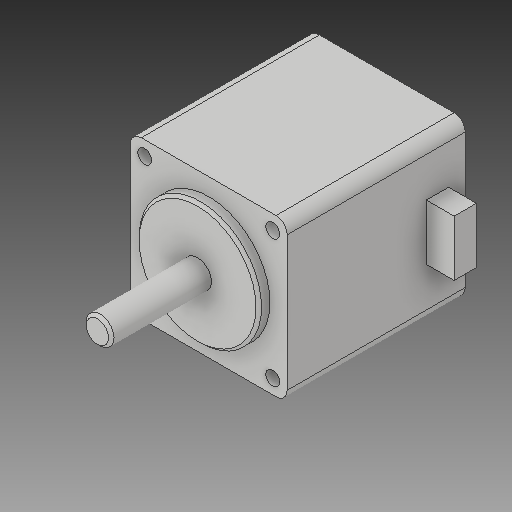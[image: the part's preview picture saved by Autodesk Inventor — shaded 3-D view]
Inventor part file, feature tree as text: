
AUTODESK INVENTOR PART (.ipt)
format: ipt  version: 2019 (Build 230136000, 136)  size: 180,736 bytes
history: native  units: mm
features: extrude x5, sketch x5, chamfer x2, fillet x1
ambient origin geometry x8: Origin, YZ Plane, XZ Plane, XY Plane, X Axis, Y Axis, Z Axis, Center Point
bodies: Solid1 (feature_tree)
feature tree (13):
  extrude  "Extrusion1"  Depth=28.2mm
  extrude  "Extrusion2"  Depth=32.0mm
  extrude  "Extrusion3"  Depth=2.5mm
  extrude  "Extrusion4"  Depth=4.5mm TaperAngle=0.0deg
  fillet  "Fillet1"  Radius=22.0mm
  chamfer  "Chamfer1"  Distance=2.0mm
  chamfer  "Chamfer2"  Distance=18.0mm
  extrude  "Extrusion5"  Depth=2.0mm
  sketch  "Sketch1"  dims[d0=28.2mm d1=28.2mm]
  sketch  "Sketch2"  dims[d2=32.0mm d3=0.0mm d4=23.0mm]
  sketch  "Sketch3"  dims[d5=23.0mm d6=2.5mm]
  sketch  "Sketch4"  dims[d7=40.0mm d9=360.0deg d11=4.5mm d12=0.0mm d13=22.0mm d14=2.0mm d15=0.0mm]
  sketch  "Sketch5"  dims[d16=5.0mm d17=18.0mm d18=0.0mm d19=2.0mm d20=0.5mm d21=2.0mm d22=45.0deg d23=0.5mm d24=2.0mm d25=45.0deg d26=5.0mm d27=4.0mm d28=10.0mm d29=5.0mm d30=0.0mm]
